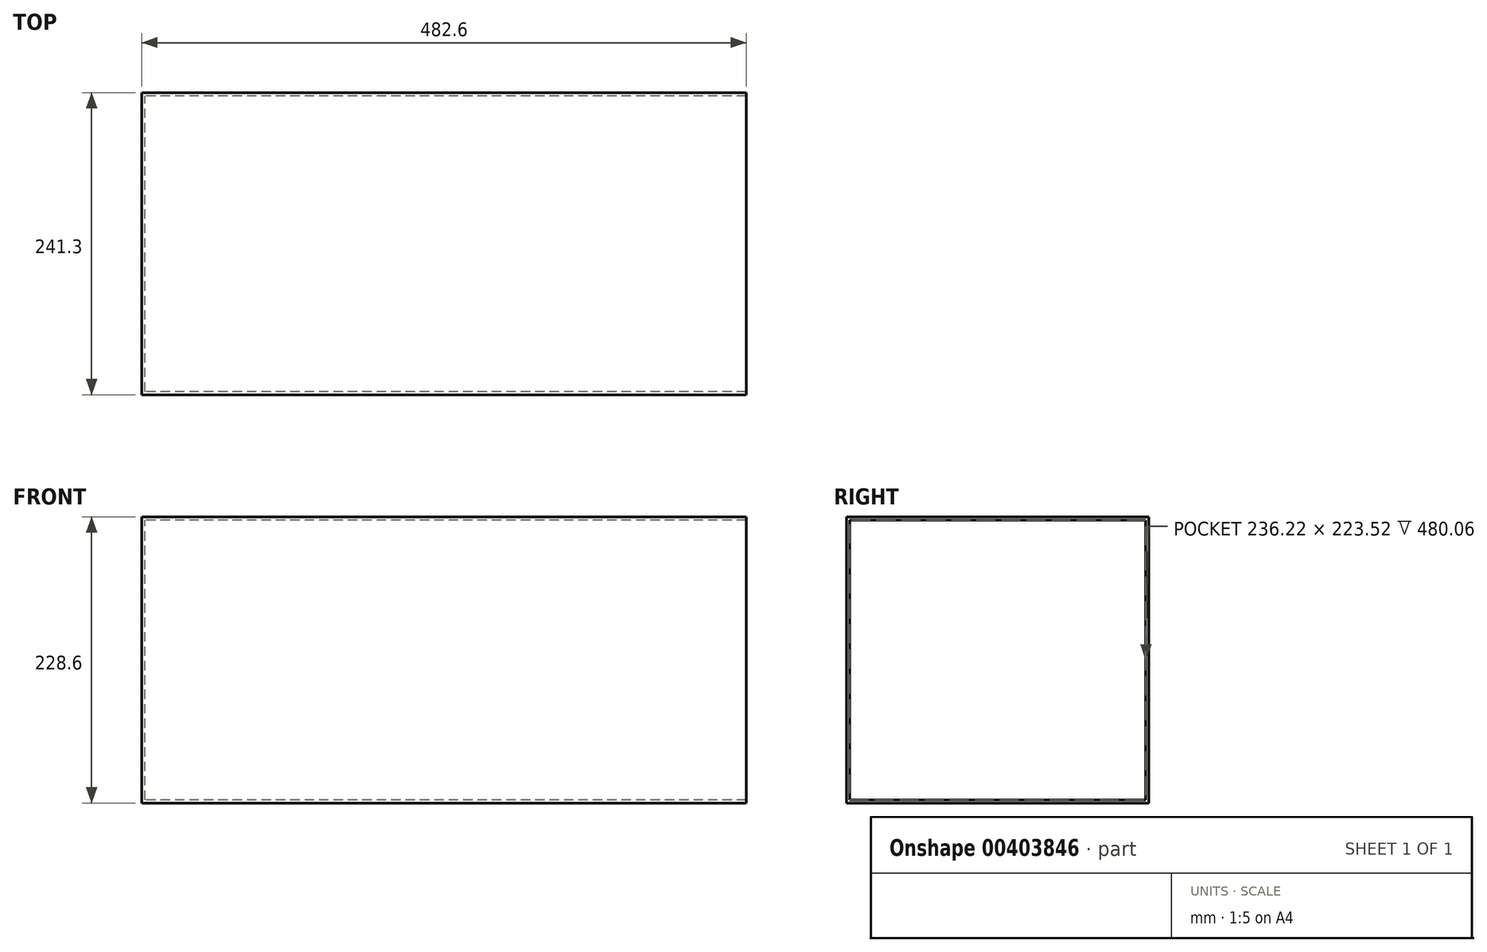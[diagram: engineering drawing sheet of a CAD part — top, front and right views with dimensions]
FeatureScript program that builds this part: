
annotation { "Feature Type Name" : "Feature", "Feature Type Description" : "" }
export const myFeature = defineFeature(function(context is Context, id is Id, definition is map)
    precondition{}
    {
        {
            var Q0;
            Q0=qCreatedBy(makeId("Front.planeOp"),FACE);
            var sketch = newSketch(context, id + "F0", { "sketchPlane" : qUnion([Q0])});
            skLineSegment(sketch, "E0.bottom", {"start": v(133.16, 0) * mm, "end": v(-349.44, 0) * mm});
            skLineSegment(sketch, "E0.top", {"start": v(133.16, 228.6) * mm, "end": v(-349.44, 228.6) * mm});
            skLineSegment(sketch, "E0.left", {"start": v(133.16, 0) * mm, "end": v(133.16, 228.6) * mm});
            skLineSegment(sketch, "E0.right", {"start": v(-349.44, 0) * mm, "end": v(-349.44, 228.6) * mm});
            skPoint(sketch, "E0.middle", {"position": v(-108.14, 114.3) * mm});
            skSolve(sketch);
        }
        {
            var Q0;
            Q0=makeQuery(id+"F0.imprint","IMPRINT",FACE,{"disambiguationData":[TD([[makeQuery(id+"F0.imprint","IMPRINT",EDGE,{"derivedFrom":sQuery(id+"F0.wireOp",EDGE,"E0.bottom")}),-1.0]])]});
            extrude(context, id + "F1", {"entities" : qUnion([Q0]), "endBound" : BoundingType.SYMMETRIC, "depth" : 25.4 * mm});
        }
        {
            var Q0;
            Q0=makeQuery(id+"F1.opExtrude","CAP_FACE",FACE,{"disambiguationData":[OSD([sQuery(id+"F0.wireOp",EDGE,"E0.bottom"),sQuery(id+"F0.wireOp",EDGE,"E0.top"),sQuery(id+"F0.wireOp",EDGE,"E0.left"),sQuery(id+"F0.wireOp",EDGE,"E0.right")])],"isStart":false});
            var Q1;
            Q1 = qSketchRegion(id + "F0", true);
            extrude(context, id + "F2", {"entities" : qUnion([Q0, Q1]), "operationType" : NewBodyOperationType.ADD, "endBound" : BoundingType.SYMMETRIC, "depth" : 228.6 * mm});
        }
        {
            var Q0;
            {var subQ0=sQuery(id+"F0.wireOp",EDGE,"E0.left");Q0=makeQuery(id+"F2.boolean.opBoolean","MERGE",FACE,{"derivedFrom":[makeQuery(id+"F1.opExtrude","SWEPT_FACE",FACE,{"disambiguationData":[OSD([subQ0])]}),makeQuery(id+"F2.opExtrude","SWEPT_FACE",FACE,{"disambiguationData":[OSD([subQ0]),TDD([makeQuery(id+"F0.imprint","IMPRINT",EDGE,{"derivedFrom":subQ0})])]}),makeQuery(id+"F2.opExtrude","SWEPT_FACE",FACE,{"disambiguationData":[OSD([subQ0]),TDD([makeQuery(id+"F1.opExtrude","CAP_EDGE",EDGE,{"disambiguationData":[OSD([subQ0])],"isStart":false})])]})]});}
            shell(context, id + "F3", {"entities" : qUnion([Q0]), "thickness" : 2.54 * mm});
        }
    });
